# Revit family: HVAC_Air-Conditioning_Friedrich_Variable-Refrigerant-Packaged-Heat-Pump_VRP24
name_source: partatom
category: Mechanical Equipment
revit_build: Autodesk Revit 2015 (Build: 20140606_1530(x64)
units: mm (PartAtom-declared; Revit-internal decimal feet)

## types (2) — shared parameters
Air Flow = 850.0 CFM
Air Supply Depth = 6.5 "
Air Supply Width = 24 "
BIMobject category = Air Conditioning
BIMobject category code = hvac-air-con
BIMobject main category = HVAC
BIMobject main category code = hvac
Brand url = http://friedrich.com
COP = 3.1
Cooling = 23400 Btu/h
Cooling Current = 10 A
Cooling Range = 12000-28000
Depth = 25.13 "
Description = Precision Inverter® compressor delivers best in class cooling performance with efficiencies up to 20 SEER. Super efficient heating with low-ambient heat pump operation to 0˚ F*.
Design country = United States
EER Rating = 11
Edition number = 1
Filter Material = Filter - Friedrich - Grey
Heating Power = 1954 W
Heating Seasonal Performance Factor = 10
Height = 62 "
IFC Classification = Air Terminal
Installation instructions = https://cdn2.hubspot.net
Load Classification = HVAC
Main Material = Metal - Friedrich - White
Manufacturer = Friedrich
Manufacturer country = Mexico
Manufacturer name = Friedrich
Masterformat 2014 Code = 23 81 13
Masterformat 2014 Description = Packaged Terminal Air-Conditioners
Material main = Metal
NBS Reference Code = 68-38
NBS Reference Description = Heat Pumps
Nominal height = 61 "
Nominal width = 26 "
OmniClass Code = 23-33 17 00
OmniClass Description = Heat Pumps
Outdoor Operating Range = 55-115
Product Guid = d43a2fee-16d1-47cf-a3c8-3c47f23168e0
Product SKU = VRP24
Product certification = https://cdn2.hubspot.net
Product data url = https://bimobject.com
Product family = Variable Refrigerant Package
Product group = VRP
Product url = https://www.friedrich.com
QR code = http://bimobject.com
Return Air Depth = 13.75 "
Return Air Width = 23.75 "
SEER = 17.5
Technical description = https://cdn2.hubspot.net
Total Heating Capacity = 21000 Btu/h
UNSPSC Code = 40101806
URL = https://www.friedrich.com
Uniclass 1.4 Code = L7524
Uniclass 1.4 Description = Heat pumps
Uniclass 2.0 Code = PR-68-38
Uniclass 2.0 Description = Heat Pumps
Uniclass 2015 Code = Pr_70_60_37
Uniclass 2015 Name = Heat pumps
Uniformat II Code = D3050
Uniformat II Description = Terminal & Package Units
Weight = 255.00 lbm
Weight Net (Kg) = 268
Width = 26.13 "
Youtube clip = https://youtu.be

## per-type parameters (varying)
| type | Heat Pump Current | Voltage | Voltage Range |
| VRP24K | 9 A | 230 V | 208-230 |
| VRP24R | 8 A | 265 V |  |

note: column(s) folded — value = type name in every type: Model

## geometry (parser evidence)
native form markers: Sweep x3
no freeform markers — native parametric forms only
